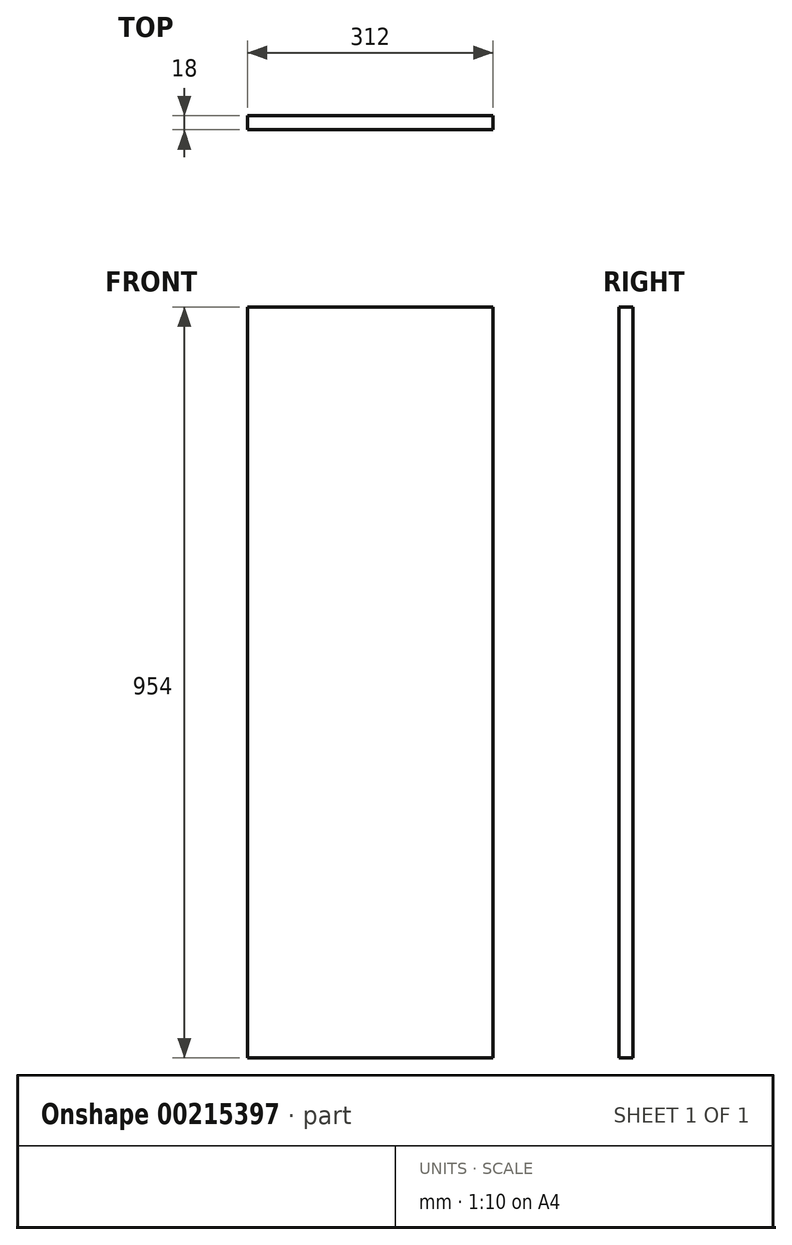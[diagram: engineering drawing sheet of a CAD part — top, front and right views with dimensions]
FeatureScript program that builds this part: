
annotation { "Feature Type Name" : "Feature", "Feature Type Description" : "" }
export const myFeature = defineFeature(function(context is Context, id is Id, definition is map)
    precondition{}
    {
        {
            var Q0;
            Q0=qCreatedBy(makeId("Front.planeOp"),FACE);
            var sketch = newSketch(context, id + "F0", { "sketchPlane" : qUnion([Q0])});
            skLineSegment(sketch, "E0.bottom", {"start": v(-156, -477) * mm, "end": v(156, -477) * mm});
            skLineSegment(sketch, "E0.top", {"start": v(-156, 477) * mm, "end": v(156, 477) * mm});
            skLineSegment(sketch, "E0.left", {"start": v(-156, -477) * mm, "end": v(-156, 477) * mm});
            skLineSegment(sketch, "E0.right", {"start": v(156, -477) * mm, "end": v(156, 477) * mm});
            skPoint(sketch, "E0.middle", {"position": v(0, 0) * mm});
            skSolve(sketch);
        }
        {
            var Q0;
            Q0=makeQuery(id+"F0.imprint","IMPRINT",FACE,{"disambiguationData":[TD([[makeQuery(id+"F0.imprint","IMPRINT",EDGE,{"derivedFrom":sQuery(id+"F0.wireOp",EDGE,"E0.bottom")}),1.0]])]});
            extrude(context, id + "F1", {"entities" : qUnion([Q0]), "depth" : 18 * mm});
        }
    });
